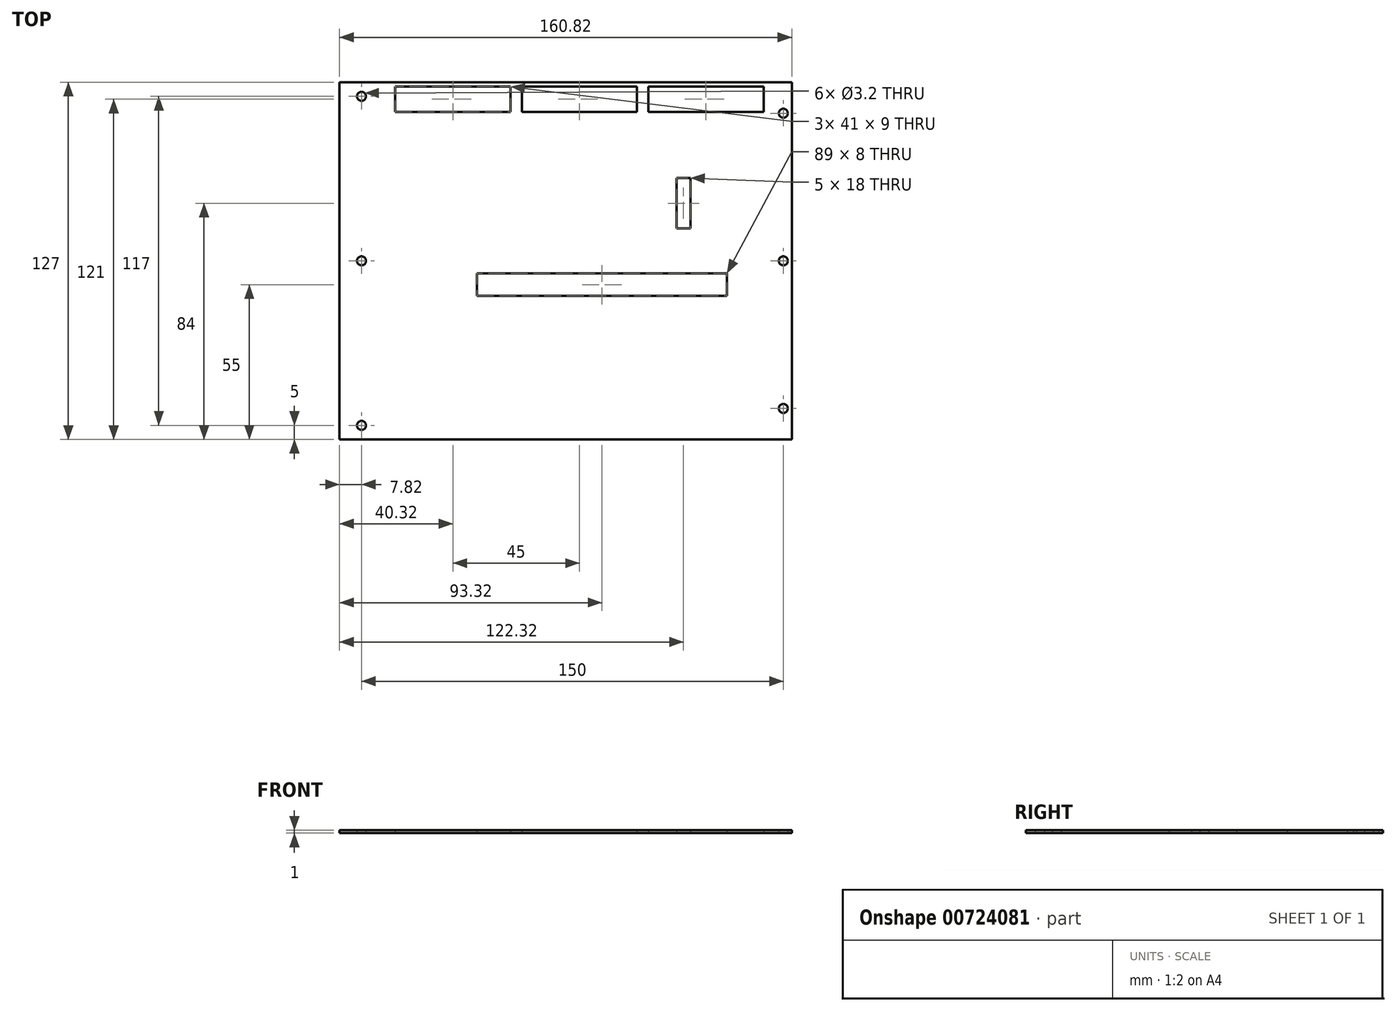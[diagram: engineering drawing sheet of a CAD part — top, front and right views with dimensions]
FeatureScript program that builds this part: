
annotation { "Feature Type Name" : "Feature", "Feature Type Description" : "" }
export const myFeature = defineFeature(function(context is Context, id is Id, definition is map)
    precondition{}
    {
        {
            var Q0;
            Q0=qCreatedBy(makeId("Top.planeOp"),FACE);
            var sketch = newSketch(context, id + "F0", { "sketchPlane" : qUnion([Q0])});
            skCircle(sketch, "E0", {"center": v(0, 58.5) * mm, "radius": 1.6 * mm});
            skCircle(sketch, "E1", {"center": v(-150, 0) * mm, "radius": 1.6 * mm});
            skCircle(sketch, "E2", {"center": v(-150, 52.5) * mm, "radius": 1.6 * mm});
            skCircle(sketch, "E3.MirrorC", {"center": v(150, 52.5) * mm, "radius": 1.6 * mm});
            skCircle(sketch, "E4.MirrorC", {"center": v(150, 0) * mm, "radius": 1.6 * mm});
            skCircle(sketch, "E5.MirrorC", {"center": v(-150, -52.5) * mm, "radius": 1.6 * mm});
            skCircle(sketch, "E6.MirrorC", {"center": v(0, -58.5) * mm, "radius": 1.6 * mm});
            skCircle(sketch, "E7.MirrorC", {"center": v(150, -52.5) * mm, "radius": 1.6 * mm});
            skLineSegment(sketch, "E8.bottom", {"start": v(130, -12.5) * mm, "end": v(41, -12.5) * mm});
            skLineSegment(sketch, "E8.top", {"start": v(130, -4.5) * mm, "end": v(41, -4.5) * mm});
            skLineSegment(sketch, "E8.left", {"start": v(130, -12.5) * mm, "end": v(130, -4.5) * mm});
            skLineSegment(sketch, "E8.right", {"start": v(41, -12.5) * mm, "end": v(41, -4.5) * mm});
            skPoint(sketch, "E8.middle", {"position": v(85.5, -8.5) * mm});
            skLineSegment(sketch, "E9.bottom", {"start": v(153, 63.5) * mm, "end": v(-153, 63.5) * mm});
            skLineSegment(sketch, "E9.top", {"start": v(153, -63.5) * mm, "end": v(-153, -63.5) * mm});
            skLineSegment(sketch, "E9.left", {"start": v(153, 63.5) * mm, "end": v(153, -63.5) * mm});
            skLineSegment(sketch, "E9.right", {"start": v(-153, 63.5) * mm, "end": v(-153, -63.5) * mm});
            skLineSegment(sketch, "E10.bottom", {"start": v(117, 11.5) * mm, "end": v(112, 11.5) * mm});
            skLineSegment(sketch, "E10.top", {"start": v(117, 29.5) * mm, "end": v(112, 29.5) * mm});
            skLineSegment(sketch, "E10.left", {"start": v(117, 11.5) * mm, "end": v(117, 29.5) * mm});
            skLineSegment(sketch, "E10.right", {"start": v(112, 11.5) * mm, "end": v(112, 29.5) * mm});
            skPoint(sketch, "E10.middle", {"position": v(114.5, 20.5) * mm});
            skLineSegment(sketch, "E11.bottom", {"start": v(-11.2, 61.2) * mm, "end": v(-27.8, 61.2) * mm});
            skLineSegment(sketch, "E11.top", {"start": v(-11.2, 44.1) * mm, "end": v(-27.8, 44.1) * mm});
            skLineSegment(sketch, "E11.left", {"start": v(-11.2, 61.2) * mm, "end": v(-11.2, 44.1) * mm});
            skLineSegment(sketch, "E11.right", {"start": v(-27.8, 61.2) * mm, "end": v(-27.8, 44.1) * mm});
            skLineSegment(sketch, "E12.bottom", {"start": v(12, 62) * mm, "end": v(53, 62) * mm});
            skLineSegment(sketch, "E12.top", {"start": v(12, 53) * mm, "end": v(53, 53) * mm});
            skLineSegment(sketch, "E12.left", {"start": v(12, 62) * mm, "end": v(12, 53) * mm});
            skLineSegment(sketch, "E12.right", {"start": v(53, 62) * mm, "end": v(53, 53) * mm});
            skLineSegment(sketch, "E13.bottom", {"start": v(57, 62) * mm, "end": v(98, 62) * mm});
            skLineSegment(sketch, "E13.top", {"start": v(57, 53) * mm, "end": v(98, 53) * mm});
            skLineSegment(sketch, "E13.left", {"start": v(57, 62) * mm, "end": v(57, 53) * mm});
            skLineSegment(sketch, "E13.right", {"start": v(98, 62) * mm, "end": v(98, 53) * mm});
            skLineSegment(sketch, "E14.bottom", {"start": v(102, 62) * mm, "end": v(143, 62) * mm});
            skLineSegment(sketch, "E14.top", {"start": v(102, 53) * mm, "end": v(143, 53) * mm});
            skLineSegment(sketch, "E14.left", {"start": v(102, 62) * mm, "end": v(102, 53) * mm});
            skLineSegment(sketch, "E14.right", {"start": v(143, 62) * mm, "end": v(143, 53) * mm});
            skLineSegment(sketch, "E15.bottom", {"start": v(-146, 62) * mm, "end": v(-92, 62) * mm});
            skLineSegment(sketch, "E15.top", {"start": v(-146, 48) * mm, "end": v(-92, 48) * mm});
            skLineSegment(sketch, "E15.left", {"start": v(-146, 62) * mm, "end": v(-146, 48) * mm});
            skLineSegment(sketch, "E15.right", {"start": v(-92, 62) * mm, "end": v(-92, 48) * mm});
            skLineSegment(sketch, "E16.bottom", {"start": v(-91, 62) * mm, "end": v(-59, 62) * mm});
            skLineSegment(sketch, "E16.top", {"start": v(-91, 48) * mm, "end": v(-59, 48) * mm});
            skLineSegment(sketch, "E16.left", {"start": v(-91, 62) * mm, "end": v(-91, 48) * mm});
            skLineSegment(sketch, "E16.right", {"start": v(-59, 62) * mm, "end": v(-59, 48) * mm});
            skLineSegment(sketch, "E17.bottom", {"start": v(-145.5, 43) * mm, "end": v(-134.5, 43) * mm});
            skLineSegment(sketch, "E17.top", {"start": v(-145.5, 8) * mm, "end": v(-134.5, 8) * mm});
            skLineSegment(sketch, "E17.left", {"start": v(-145.5, 43) * mm, "end": v(-145.5, 8) * mm});
            skLineSegment(sketch, "E17.right", {"start": v(-134.5, 43) * mm, "end": v(-134.5, 8) * mm});
            skCircle(sketch, "E18", {"center": v(0, 0) * mm, "radius": 1.6 * mm});
            skSolve(sketch);
        }
        {
            var Q0;
            Q0 = qSketchRegion(id + "F0", true);
            extrude(context, id + "F1", {"entities" : qUnion([Q0]), "depth" : 1 * mm, "offsetDistance" : 25 * mm});
        }
        {
            var Q0;
            Q0=qCreatedBy(makeId("Top.planeOp"),FACE);
            var sketch = newSketch(context, id + "F2", { "sketchPlane" : qUnion([Q0])});
            skLineSegment(sketch, "E19.bottom", {"start": v(-7.82, 69.9) * mm, "end": v(-156.06, 69.9) * mm});
            skLineSegment(sketch, "E19.top", {"start": v(-7.82, -69.4) * mm, "end": v(-156.06, -69.4) * mm});
            skLineSegment(sketch, "E19.left", {"start": v(-7.82, 69.9) * mm, "end": v(-7.82, -69.4) * mm});
            skLineSegment(sketch, "E19.right", {"start": v(-156.06, 69.9) * mm, "end": v(-156.06, -69.4) * mm});
            skSolve(sketch);
        }
        {
            var Q0;
            Q0 = qSketchRegion(id + "F2", true);
            extrude(context, id + "F3", {"entities" : qUnion([Q0]), "operationType" : NewBodyOperationType.REMOVE, "endBound" : BoundingType.SYMMETRIC, "depth" : 25 * mm, "offsetDistance" : 25 * mm});
        }
    });
